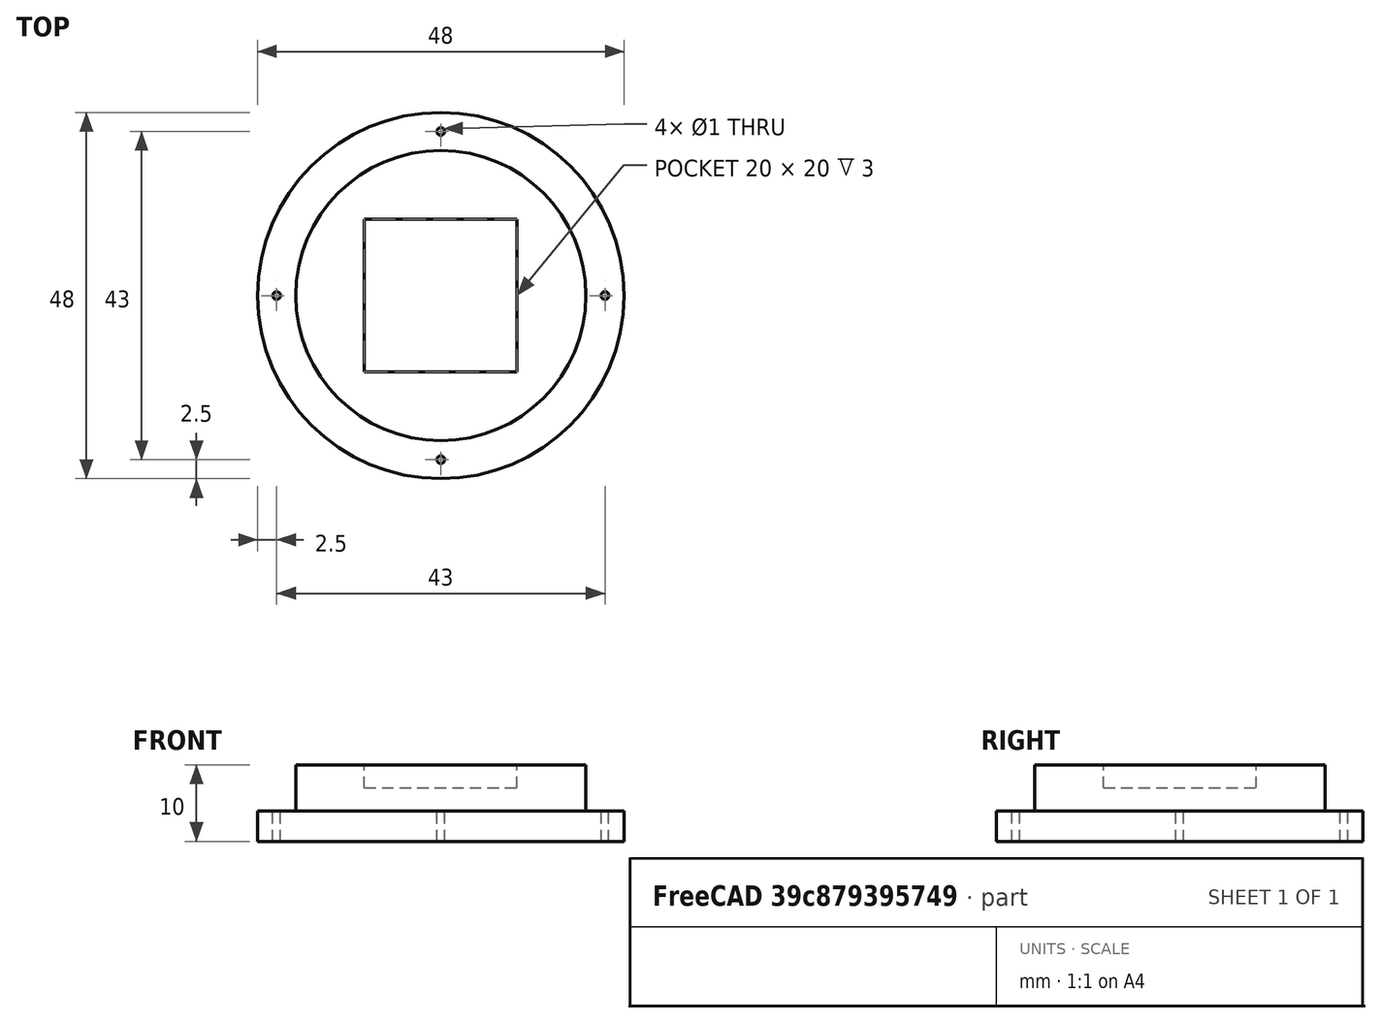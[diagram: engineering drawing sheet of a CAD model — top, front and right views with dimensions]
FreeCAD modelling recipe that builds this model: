
FCSTD DOCUMENT  (FreeCAD 0.19R)
Label: sockel
License: All rights reserved
LicenseURL: http://en.wikipedia.org/wiki/All_rights_reserved
objects: Part::Cylinder×4, Part::Part2DObjectPython×2, Part::Extrusion×2, Part::MultiFuse×2, Part::Cut×2, Part::Box×1
note: 13 computed .brp shape members not serialized (recipe doc carries the construction recipe); baked Part::Feature solids carry a one-line shape summary decoded from their .brp

FEATURE [Part::Part2DObjectPython] Circle  # Draft 2D object (typed FeaturePython)
  Area = 1809.56
  FirstAngle = 0
  LastAngle = 0
  MakeFace = true
  Radius = 24
FEATURE [Part::Extrusion] Extrude
  Base = -> Circle
  Dir = (0,0,1)
  DirMode = 2
  FaceMakerClass = Part::FaceMakerBullseye
  LengthFwd = 4
  LengthRev = 0
  Solid = false
  Symmetric = false
FEATURE [Part::Part2DObjectPython] Circle001  # Draft 2D object (typed FeaturePython)
  Area = 1134.11
  FirstAngle = 0
  LastAngle = 0
  MakeFace = true
  Radius = 19
FEATURE [Part::Extrusion] Extrude001
  Base = -> Circle001
  Dir = (0,0,1)
  DirMode = 2
  FaceMakerClass = Part::FaceMakerBullseye
  LengthFwd = 10
  LengthRev = 0
  Solid = false
  Symmetric = false
FEATURE [Part::Cylinder] Cylinder
  Angle = 360
  AttacherType = Attacher::AttachEngine3D
  Height = 10
  Placement = pos=(21.5,0,-3) rot=(0,0,1;0rad)
  Radius = 0.5
FEATURE [Part::Cylinder] Cylinder001
  Angle = 360
  AttacherType = Attacher::AttachEngine3D
  Height = 10
  Placement = pos=(-21.5,0,-3) rot=(0,0,1;0rad)
  Radius = 0.5
FEATURE [Part::Cylinder] Cylinder002
  Angle = 360
  AttacherType = Attacher::AttachEngine3D
  Height = 10
  Placement = pos=(0,21.5,-3) rot=(0,0,1;0rad)
  Radius = 0.5
FEATURE [Part::Cylinder] Cylinder003
  Angle = 360
  AttacherType = Attacher::AttachEngine3D
  Height = 10
  Placement = pos=(0,-21.5,-3) rot=(0,0,1;0rad)
  Radius = 0.5
FEATURE [Part::MultiFuse] Fusion
  Shapes = -> [Cylinder,Cylinder001,Cylinder002,Cylinder003]
FEATURE [Part::Cut] Cut
  Base = -> Extrude
  Tool = -> Fusion
FEATURE [Part::Box] Box  label="Cube"
  AttacherType = Attacher::AttachEngine3D
  Height = 20
  Length = 20
  Placement = pos=(-10,-10,7) rot=(0,0,1;0rad)
  Width = 20
FEATURE [Part::MultiFuse] Fusion001
  Shapes = -> [Cut,Extrude001]
FEATURE [Part::Cut] Cut001
  Base = -> Fusion001
  Tool = -> Box
